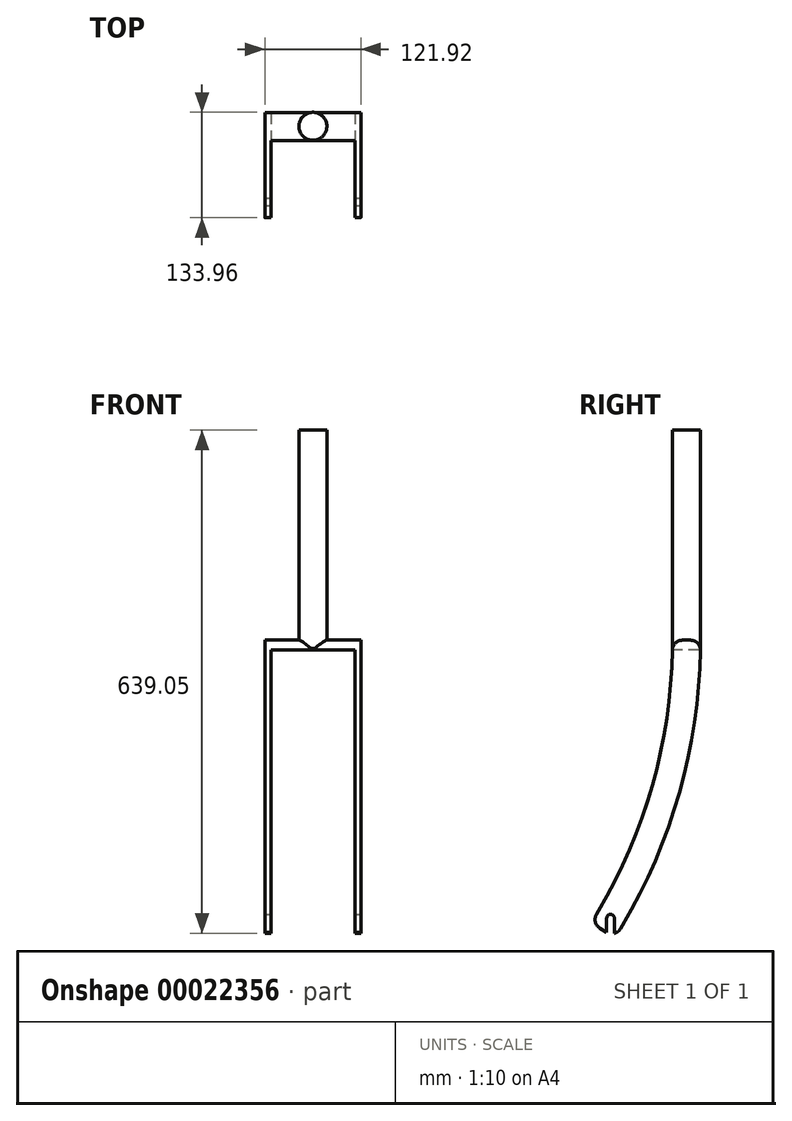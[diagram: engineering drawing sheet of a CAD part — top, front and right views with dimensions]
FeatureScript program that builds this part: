
annotation { "Feature Type Name" : "Feature", "Feature Type Description" : "" }
export const myFeature = defineFeature(function(context is Context, id is Id, definition is map)
    precondition{}
    {
        {
            var Q0;
            Q0=qCreatedBy(makeId("Right.planeOp"),FACE);
            var sketch = newSketch(context, id + "F0", { "sketchPlane" : qUnion([Q0])});
            skArc(sketch, "E0", {"start": v(-111.83, -344.01) * mm, "mid": v(-43.39, -184.32) * mm, "end": v(-17.9, -12.47) * mm});
            skArc(sketch, "E1", {"start": v(-96.52, -353.06) * mm, "mid": v(-24.56, -183) * mm, "end": v(0, 0) * mm, "construction": true});
            skArc(sketch, "E2", {"start": v(-81.21, -362.1) * mm, "mid": v(-9.15, -193.93) * mm, "end": v(17.66, -12.93) * mm});
            skLineSegment(sketch, "E3", {"start": v(-5.2, 0) * mm, "end": v(4.96, 0) * mm});
            skLineSegment(sketch, "E4", {"start": v(-111.83, -344.01) * mm, "end": v(-81.21, -362.1) * mm, "construction": true});
            skLineSegment(sketch, "E5", {"start": v(0, 0) * mm, "end": v(0, 266.7) * mm, "construction": true});
            skLineSegment(sketch, "E6", {"start": v(-149.62, -442.92) * mm, "end": v(-136.7, -421.05) * mm, "construction": true});
            skLineSegment(sketch, "E7", {"start": v(-111.83, -344.01) * mm, "end": v(-114.41, -348.39) * mm});
            skLineSegment(sketch, "E8", {"start": v(-81.21, -362.1) * mm, "end": v(-83.8, -366.48) * mm});
            skLineSegment(sketch, "E9", {"start": v(-109.94, -365.78) * mm, "end": v(-101.2, -370.95) * mm});
            skPoint(sketch, "E10.visualSharp", {"position": v(-120.87, -359.32) * mm});
            skArc(sketch, "E10.filletArc", {"start": v(-114.41, -348.39) * mm, "mid": v(-115.78, -358.01) * mm, "end": v(-109.94, -365.78) * mm});
            skPoint(sketch, "E11.visualSharp", {"position": v(-90.26, -377.41) * mm});
            skArc(sketch, "E11.filletArc", {"start": v(-101.2, -370.95) * mm, "mid": v(-91.57, -372.32) * mm, "end": v(-83.8, -366.48) * mm});
            skPoint(sketch, "E12.visualSharp", {"position": v(-17.78, 0) * mm});
            skArc(sketch, "E12.filletArc", {"start": v(-5.2, 0) * mm, "mid": v(-14.1, -3.64) * mm, "end": v(-17.9, -12.47) * mm});
            skPoint(sketch, "E13.visualSharp", {"position": v(17.78, 0) * mm});
            skArc(sketch, "E13.filletArc", {"start": v(17.66, -12.93) * mm, "mid": v(14.03, -3.8) * mm, "end": v(4.96, 0) * mm});
            skSolve(sketch);
        }
        {
            var Q0;
            Q0 = qSketchRegion(id + "F0", true);
            extrude(context, id + "F1", {"entities" : qUnion([Q0]), "endBound" : BoundingType.SYMMETRIC, "depth" : 121.92 * mm});
        }
        {
            var Q0;
            Q0=qCreatedBy(makeId("Right.planeOp"),FACE);
            var sketch = newSketch(context, id + "F2", { "sketchPlane" : qUnion([Q0])});
            skLineSegment(sketch, "E14", {"start": v(-101.35, -372.72) * mm, "end": v(-101.35, -353.06) * mm});
            skArc(sketch, "E15", {"start": v(-101.35, -353.06) * mm, "mid": v(-96.52, -348.23) * mm, "end": v(-91.7, -353.06) * mm});
            skLineSegment(sketch, "E16", {"start": v(-91.7, -353.06) * mm, "end": v(-91.7, -372.72) * mm});
            skLineSegment(sketch, "E17", {"start": v(-101.35, -372.72) * mm, "end": v(-91.7, -372.72) * mm});
            skSolve(sketch);
        }
        {
            var Q0;
            Q0 = qSketchRegion(id + "F2", true);
            extrude(context, id + "F3", {"entities" : qUnion([Q0]), "operationType" : NewBodyOperationType.REMOVE, "endBound" : BoundingType.THROUGH_ALL, "oppositeDirection" : true, "depth" : 25.4 * mm, "hasSecondDirection" : true, "secondDirectionBound" : SecondDirectionBoundingType.THROUGH_ALL, "secondDirectionOppositeDirection" : false, "secondDirectionDepth" : 25.4 * mm});
        }
        {
            var Q0;
            Q0=qCreatedBy(makeId("Front.planeOp"),FACE);
            var sketch = newSketch(context, id + "F4", { "sketchPlane" : qUnion([Q0])});
            skLineSegment(sketch, "E18", {"start": v(-53.34, -12.7) * mm, "end": v(-53.34, -393.7) * mm});
            skLineSegment(sketch, "E19", {"start": v(-53.34, -12.7) * mm, "end": v(53.34, -12.7) * mm});
            skLineSegment(sketch, "E20", {"start": v(53.34, -12.7) * mm, "end": v(53.34, -393.7) * mm});
            skLineSegment(sketch, "E21", {"start": v(-53.34, -393.7) * mm, "end": v(53.34, -393.7) * mm});
            skSolve(sketch);
        }
        {
            var Q0;
            Q0 = qSketchRegion(id + "F4", true);
            extrude(context, id + "F5", {"entities" : qUnion([Q0]), "operationType" : NewBodyOperationType.REMOVE, "endBound" : BoundingType.THROUGH_ALL, "oppositeDirection" : true, "depth" : 25.4 * mm, "hasSecondDirection" : true, "secondDirectionBound" : SecondDirectionBoundingType.THROUGH_ALL, "secondDirectionOppositeDirection" : false, "secondDirectionDepth" : 25.4 * mm});
        }
        {
            var Q0;
            Q0=qCreatedBy(makeId("Top.planeOp"),FACE);
            var sketch = newSketch(context, id + "F6", { "sketchPlane" : qUnion([Q0])});
            skCircle(sketch, "E22", {"center": v(0, 0) * mm, "radius": 17.78 * mm});
            skSolve(sketch);
        }
        {
            var Q0;
            Q0 = qSketchRegion(id + "F6", true);
            var Q1;
            Q1=makeQuery(id+"F5.boolean.opBoolean","COPY",FACE,{"derivedFrom":makeQuery(id+"F5.opExtrude","SWEPT_FACE",FACE,{"disambiguationData":[OSD([sQuery(id+"F4.wireOp",EDGE,"E19")])]})});
            extrude(context, id + "F7", {"entities" : qUnion([Q0]), "operationType" : NewBodyOperationType.ADD, "depth" : 266.7 * mm, "hasSecondDirection" : true, "secondDirectionOppositeDirection" : true, "secondDirectionBoundEntityFace" : qUnion([Q1]), "secondDirectionDepth" : 12.7 * mm});
        }
    });
